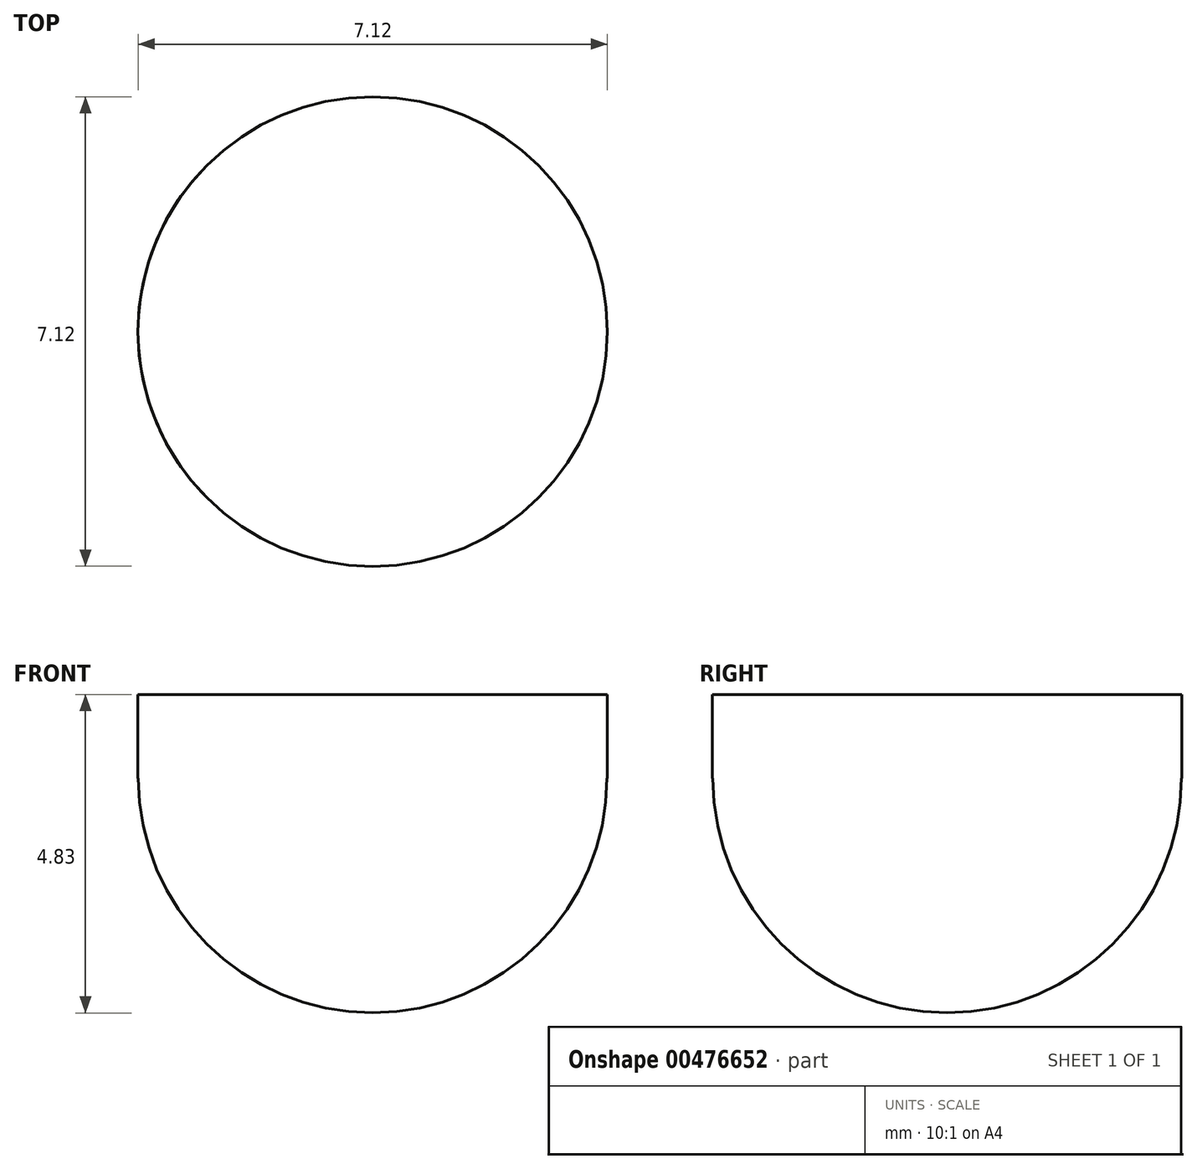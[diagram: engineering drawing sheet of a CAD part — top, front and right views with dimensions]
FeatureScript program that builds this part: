
annotation { "Feature Type Name" : "Feature", "Feature Type Description" : "" }
export const myFeature = defineFeature(function(context is Context, id is Id, definition is map)
    precondition{}
    {
        {
            var Q0;
            Q0=qCreatedBy(makeId("Top.planeOp"),FACE);
            var sketch = newSketch(context, id + "F0", { "sketchPlane" : qUnion([Q0])});
            skArc(sketch, "E0", {"start": v(0, -3.68) * mm, "mid": v(3.56, -0.12) * mm, "end": v(0, 3.43) * mm});
            skLineSegment(sketch, "E1", {"start": v(0, -3.68) * mm, "end": v(0, 3.43) * mm});
            skSolve(sketch);
        }
        {
            var Q0;
            Q0 = qSketchRegion(id + "F0", true);
            var Q1;
            Q1=sQuery(id+"F0.wireOp",EDGE,"E1");
            revolve(context, id + "F1", {"entities" : qUnion([Q0]), "axis" : qUnion([Q1]), "revolveType" : RevolveType.ONE_DIRECTION, "angle" : 180 * degree});
        }
        {
            var Q0;
            Q0=makeQuery(id+"F1.opRevolve","CAP_FACE",FACE,{"disambiguationData":[OSD([sQuery(id+"F0.wireOp",EDGE,"E0"),sQuery(id+"F0.wireOp",EDGE,"E1")])],"isStart":true});
            var sketch = newSketch(context, id + "F2", { "sketchPlane" : qUnion([Q0])});
            skCircle(sketch, "E2", {"center": v(0, -0.12) * mm, "radius": 3.56 * mm});
            skSolve(sketch);
        }
        {
            var Q0;
            Q0 = qSketchRegion(id + "F2", true);
            extrude(context, id + "F3", {"entities" : qUnion([Q0]), "operationType" : NewBodyOperationType.ADD, "depth" : 1.27 * mm});
        }
    });
